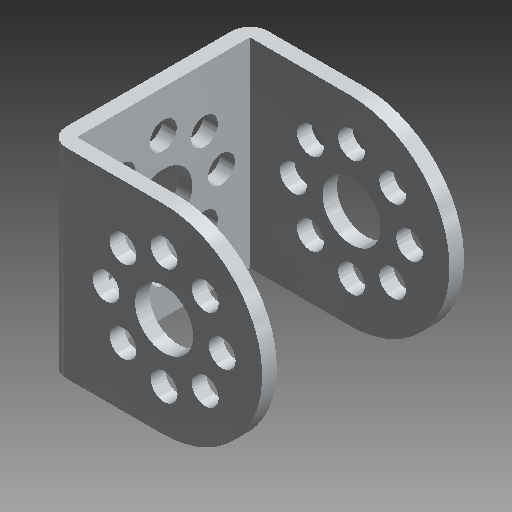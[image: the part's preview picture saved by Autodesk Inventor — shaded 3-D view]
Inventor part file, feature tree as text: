
AUTODESK INVENTOR PART (.ipt)
format: ipt  version: 2019 (Build 230136000, 136)  size: 179,200 bytes
history: native  units: mm (DEFAULTED — no unit token found)
features: fillet x1
ambient origin geometry x8: Origin, YZ Plane, XZ Plane, XY Plane, X Axis, Y Axis, Z Axis, Center Point
bodies: Solid1 (feature_tree)
feature tree (1):
  fillet  "Fillet2"  [1 undecoded]
note: 1 required parameter value undecoded (feature->parameter linkage not recoverable at this tier; creation-order binding heuristic only, values carry confidence <= 0.55)
